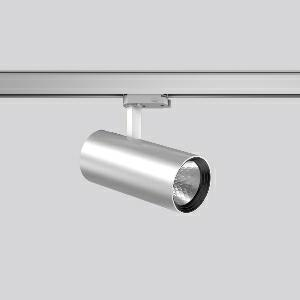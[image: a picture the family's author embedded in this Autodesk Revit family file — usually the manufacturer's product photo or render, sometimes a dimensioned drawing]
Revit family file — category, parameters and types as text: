
# Revit family: deecos_s_mini_742205_004_3_c498
name_source: partatom
category: Lighting Fixtures
units: mm (PartAtom-declared; Revit-internal decimal feet)

## family parameters
Cut with Voids When Loaded = No
Host = Face
Light Source = No
Part Type = Normal
Room Calculation Point = No
Round Connector Dimension = Use Diameter
Shared = No

## types (1)
- DEECOS S mini (1 x LED Modul 935, 3800 lm, 3500)
    Apparent Load = 29 VA
    Approval mark = CE
    CIE Flux Codes = 95 99 100 100 100
    Color Rendering = 92
    Color Temperature = 3500
    Default Elevation = 1800 mm
    Description = Series: DEECOS S mini
LED surface-mounted projector in modern design with no visible cooling ribs. Housing: die-cast aluminium, powder-coated. Rotation range: 356°. Swivel range: 90°. Black plastic ring and recessed LED to prevent glare from the side. Optical assembly with reflector made of MIRO-Silver with 98% total light reflection for outstanding efficiency - can be changed without tools. Best colour rendering index Ra>90. With multi adaptor for 3-circuit tracks 230 V. Suitable for Track on ceiling, Wall track. High quality converter without flickering and stroboscopic effect. The following accessories can be mounted without use of tools: interchangeable lenses, decorative glasses, honeycomb louvre, clear and frosted diffusers, white interchangeable plastic ring. 
Colour: silver
Diameter: 87 mm
Height: 214 mm
Lamp: LED
Socket: without socket
Colour temperature: 3500K
Colour rendering index (CRI): 92
System power: 29 W
Rated luminous flux: 3800 lm
Luminous efficiency: 131 lm/W
Control gear: Regulated power supply
Protection class: I
Type of protection: IP 20
    Height = 214 mm
    Lamp = 1 x LED Modul 935
    Lamp Light Flux = 3800 lm
    Lamp count = 1
    Length = 87 mm
    Lifetime = 50000 h
    Luminous efficacy = 131 lm/W
    Manufacturer = RZB
    ModVariant = No
    Model = 742205.004.3
    Mounting Place = Ceiling
    Mounting Type = Rail mounted
    Number of Poles = 1
    OnlyDefault = Yes
    Power Factor = 1
    Product Name = DEECOS S mini
    Product group = Track mounted projectors
    ProductGroupID = 301
    Protection Class = Protection class I
    Protection Degree = IP 20
    RLX_Detail_Level = 1
    RLX_Emergency_Light_Flux = 0 lm
    RLX_Emergency_Type = 0
    RLX_Emergency_Type_DB = No
    RlxData = <blob elided: 37305 chars, md5=7df8cd57>
    Socket = socket
    Standby Power = 0 W
    System Light Flux = 3800 lm
    System Power = 29 W
    Type Comments = Product without accessories
    Type Image = 741926.004.jpg
    URL = http://relux.com
    VarID = ---
    Voltage = 230 V
    Voltage Range = 220-240 V
    Weight = 0.00 kg
    Width = 0 mm  [stored 0 ft]

note: [stored X ft] marks values corroborated as IEEE doubles in the binary element streams (Revit-internal decimal feet)

## geometry (parser evidence)
native form markers: Blend x4, Sweep x12
no freeform markers — native parametric forms only
